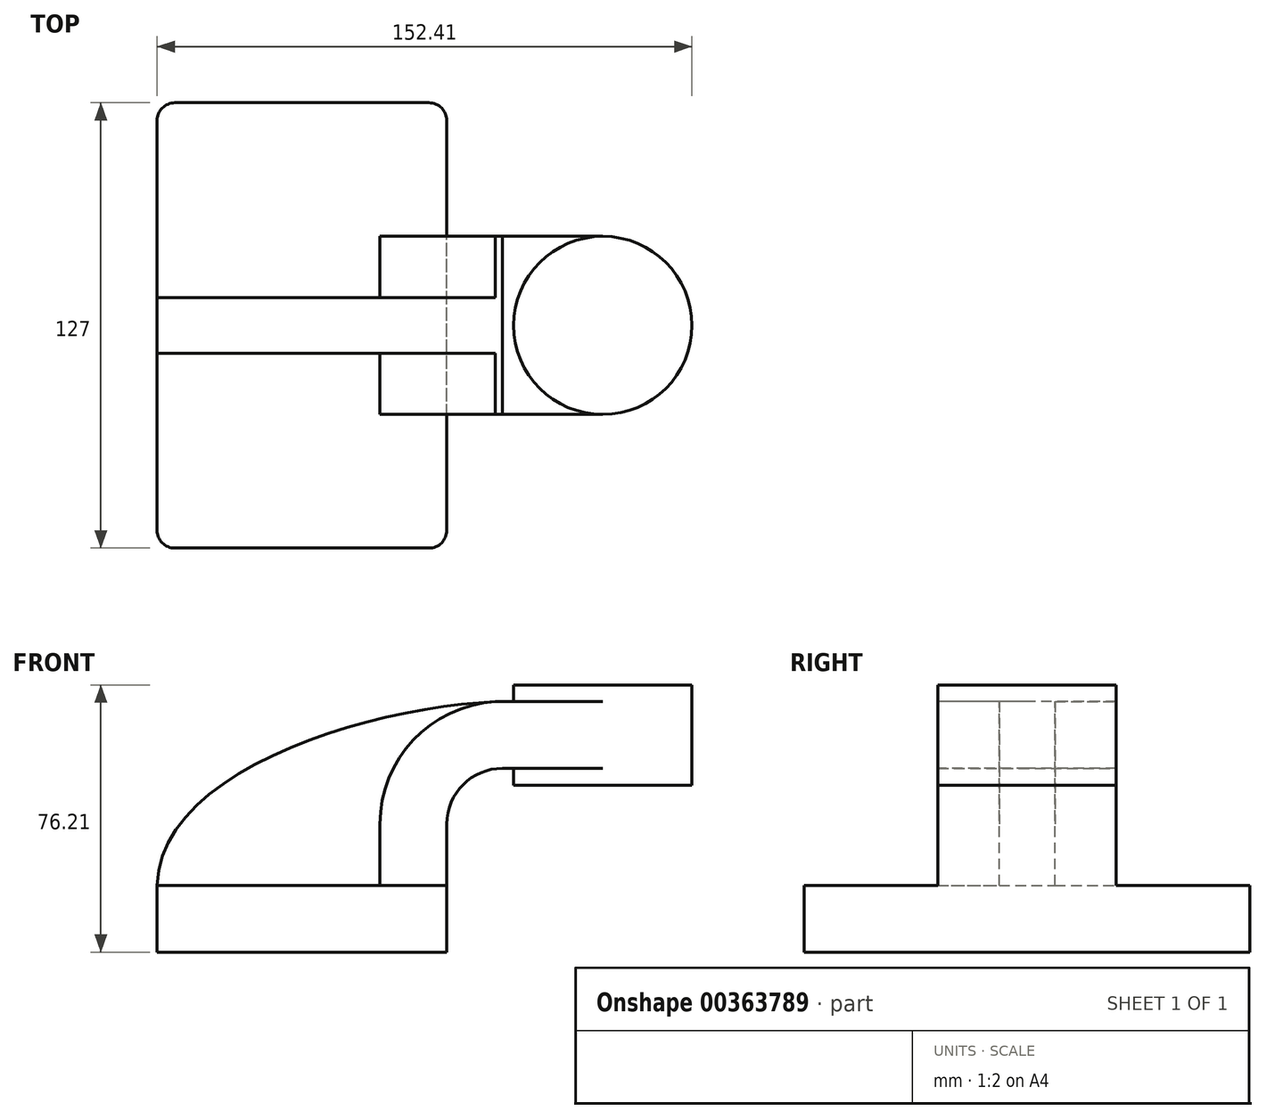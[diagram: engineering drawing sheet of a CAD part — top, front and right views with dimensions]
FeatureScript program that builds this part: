
annotation { "Feature Type Name" : "Feature", "Feature Type Description" : "" }
export const myFeature = defineFeature(function(context is Context, id is Id, definition is map)
    precondition{}
    {
        {
            var Q0;
            Q0=qCreatedBy(makeId("Front.planeOp"),FACE);
            var sketch = newSketch(context, id + "F0", { "sketchPlane" : qUnion([Q0])});
            skLineSegment(sketch, "E0.bottom", {"start": v(-41.28, -9.53) * mm, "end": v(41.28, -9.53) * mm});
            skLineSegment(sketch, "E0.top", {"start": v(-41.28, 9.52) * mm, "end": v(41.28, 9.52) * mm});
            skLineSegment(sketch, "E0.left", {"start": v(-41.28, -9.53) * mm, "end": v(-41.28, 9.52) * mm});
            skLineSegment(sketch, "E0.right", {"start": v(41.28, -9.53) * mm, "end": v(41.28, 9.52) * mm});
            skPoint(sketch, "E0.middle", {"position": v(0, 0) * mm});
            skLineSegment(sketch, "E1.bottom", {"start": v(60.32, 38.1) * mm, "end": v(111.12, 38.1) * mm});
            skLineSegment(sketch, "E1.top", {"start": v(60.32, 66.67) * mm, "end": v(111.12, 66.67) * mm});
            skLineSegment(sketch, "E1.left", {"start": v(60.32, 38.1) * mm, "end": v(60.32, 66.67) * mm});
            skLineSegment(sketch, "E1.right", {"start": v(111.13, 38.1) * mm, "end": v(111.12, 66.67) * mm});
            skPoint(sketch, "E1.middle", {"position": v(85.72, 52.39) * mm});
            skLineSegment(sketch, "E2", {"start": v(41.27, 9.52) * mm, "end": v(41.27, 27) * mm});
            skArc(sketch, "E3", {"start": v(41.27, 27) * mm, "mid": v(45.92, 38.23) * mm, "end": v(57.15, 42.88) * mm});
            skLineSegment(sketch, "E4", {"start": v(57.15, 42.88) * mm, "end": v(85.72, 42.88) * mm});
            skLineSegment(sketch, "E5.0", {"start": v(57.15, 61.93) * mm, "end": v(85.72, 61.93) * mm});
            skArc(sketch, "E5.1", {"start": v(22.22, 27) * mm, "mid": v(32.45, 51.7) * mm, "end": v(57.15, 61.93) * mm});
            skLineSegment(sketch, "E5.2", {"start": v(22.23, 9.52) * mm, "end": v(22.23, 27) * mm});
            skPoint(sketch, "E6", {"position": v(85.72, 38.1) * mm});
            skLineSegment(sketch, "E7", {"start": v(85.72, 38.1) * mm, "end": v(85.72, 66.67) * mm});
            skFitSpline(sketch, "E8", {"points": [v(-41.28, 9.53) * mm, v(57.15, 61.93) * mm], "startDerivative": vector(1.75, 101.34) * mm, "endDerivative": vector(103.13, 2.1) * mm});
            skSolve(sketch);
        }
        {
            var Q0;
            Q0=makeQuery(id+"F0.imprint","IMPRINT",FACE,{"disambiguationData":[TD([[makeQuery(id+"F0.imprint","IMPRINT",EDGE,{"derivedFrom":sQuery(id+"F0.wireOp",EDGE,"E0.bottom")}),1.0]])]});
            extrude(context, id + "F1", {"entities" : qUnion([Q0]), "endBound" : BoundingType.SYMMETRIC, "depth" : 127 * mm});
        }
        {
            var Q0;
            {var subQ1=sQuery(id+"F0.wireOp",EDGE,"E2");Q0=makeQuery(id+"F0.imprint","IMPRINT",FACE,{"disambiguationData":[TD([[makeQuery(id+"F0.imprint","IMPRINT",EDGE,{"derivedFrom":subQ1}),1.0]])]});}
            var Q1;
            {var subQ0=sQuery(id+"F0.wireOp",EDGE,"E4");var subQ1=sQuery(id+"F0.wireOp",EDGE,"E1.left");var subQ2=makeQuery(id+"F0.imprint","INTERSECT",VERTEX,{"derivedFrom":[subQ1,subQ0]});Q1=makeQuery(id+"F0.imprint","IMPRINT",FACE,{"disambiguationData":[TD([[makeQuery(id+"F0.imprint","IMPRINT",EDGE,{"disambiguationData":[TD([[subQ2,-1.0]])],"derivedFrom":subQ1}),-1.0]])]});}
            extrude(context, id + "F2", {"entities" : qUnion([Q0, Q1]), "operationType" : NewBodyOperationType.ADD, "endBound" : BoundingType.SYMMETRIC, "depth" : 50.8 * mm});
        }
        {
            var Q0;
            {var subQ3=sQuery(id+"F0.wireOp",EDGE,"E5.2");Q0=makeQuery(id+"F0.imprint","IMPRINT",FACE,{"disambiguationData":[TD([[makeQuery(id+"F0.imprint","IMPRINT",EDGE,{"derivedFrom":subQ3}),1.0]])]});}
            extrude(context, id + "F3", {"entities" : qUnion([Q0]), "operationType" : NewBodyOperationType.ADD, "endBound" : BoundingType.SYMMETRIC, "depth" : 15.88 * mm});
        }
        {
            var Q0;
            {var subQ4=sQuery(id+"F0.wireOp",EDGE,"E1.right");Q0=makeQuery(id+"F0.imprint","IMPRINT",FACE,{"disambiguationData":[TD([[makeQuery(id+"F0.imprint","IMPRINT",EDGE,{"derivedFrom":subQ4}),1.0]])]});}
            var Q1;
            Q1=sQuery(id+"F0.wireOp",EDGE,"E7");
            revolve(context, id + "F4", {"operationType" : NewBodyOperationType.ADD, "entities" : qUnion([Q0]), "axis" : qUnion([Q1]), "revolveType" : RevolveType.FULL});
        }
        {
            var Q0;
            Q0=makeQuery(id+"F1.opExtrude","CAP_EDGE",EDGE,{"disambiguationData":[OSD([sQuery(id+"F0.wireOp",EDGE,"E0.right")])],"isStart":false});
            var Q1;
            Q1=makeQuery(id+"F1.opExtrude","CAP_EDGE",EDGE,{"disambiguationData":[OSD([sQuery(id+"F0.wireOp",EDGE,"E0.left")])],"isStart":false});
            var Q2;
            Q2=makeQuery(id+"F1.opExtrude","CAP_EDGE",EDGE,{"disambiguationData":[OSD([sQuery(id+"F0.wireOp",EDGE,"E0.left")])],"isStart":true});
            var Q3;
            Q3=makeQuery(id+"F1.opExtrude","CAP_EDGE",EDGE,{"disambiguationData":[OSD([sQuery(id+"F0.wireOp",EDGE,"E0.right")])],"isStart":true});
            fillet(context, id + "F5", {"entities" : qUnion([Q0, Q1, Q2, Q3]), "radius" : 5.08 * mm, "tangentPropagation" : true, "allowEdgeOverflow" : false});
        }
    });
